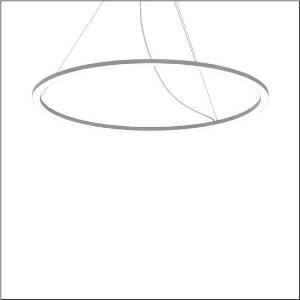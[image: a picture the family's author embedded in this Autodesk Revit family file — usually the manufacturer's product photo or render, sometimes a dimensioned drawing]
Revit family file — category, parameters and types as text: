
# Revit family: silica_r__21_ring-d_5pjbd4d3204a_8650
name_source: partatom
category: Lighting Fixtures
units: mm (PartAtom-declared; Revit-internal decimal feet)

## family parameters
Cut with Voids When Loaded = No
Host = Face
Light Source = No
Part Type = Normal
Room Calculation Point = No
Round Connector Dimension = Use Diameter
Shared = No

## types (1)
- Silica® 21 Ring-D (1 x LED, 11350 lm, 125 W, 4000K)
    Apparent Load = 125 VA
    CIE Flux Codes = 37 69 92 100 100
    Color Rendering = 80
    Color Temperature = 4000K
    Default Elevation = 1800 mm
    Description = Silica® 21 Ring-D, suspended luminaire, of PMMA, frosted, light emission: ring underside luminous distribution, primary light characteristic: symmetric, installation type: suspended mounting, LED, rated luminous flux: 11.350lm, luminous efficacy: 91lm/W, light colour: 840, colour temperature: 4000K, with terminal, 5-pole, mains connection: 230V, AC/DC, 0/50..60Hz, rated input power: 125W, housing, of extruded aluminium section, metallic grey (RAL 9006), diameter: 1.450mm, ceiling canopy, metallic grey (RAL 9006), protection rating (lamp compartment): IP40, insulation class (complete): insulation class I (protective earthing), certification: CE, impact resistance: IK02, permissible operating ambient temperature: 0..+35°C, packaging unit: 1 piece
    Height = 25 mm  [stored 0.082021 ft]
    Lamp = 1 x LED
    Lamp Light Flux = 11350 lm
    Lamp Power = 125 W
    Lamp count = 1
    Length = 1450 mm
    Luminous efficacy = 91 lm/W
    Manufacturer = Siteco
    ModVariant = No
    Model = 5PJBD4D3204A
    Mounting Place = Ceiling
    Mounting Type = Pendant
    Number of Poles = 1
    OnlyDefault = Yes
    Power Factor = 1
    Product Name = Silica® 21 Ring-D
    Product group = suspended luminaire
    ProductGroupID = 904
    Protection Class = Protection class I
    Protection Degree = IP 40
    RLX_Detail_Level = 1
    RLX_Emergency_Light_Flux = 0 lm
    RLX_Emergency_Type = 0
    RLX_Emergency_Type_DB = No
    RlxData = <blob elided: 17913 chars, md5=cb68c245>
    Socket = socket
    Standby Power = 0 W
    System Light Flux = 11350 lm
    System Power = 125 W
    Type Comments = Product without accessories
    Type Image = l_1251748.jpg
    URL = http://relux.com
    VarID = ---
    Voltage = 0 V
    Weight = 0.00 kg
    Width = 0 mm  [stored 0 ft]

note: [stored X ft] marks values corroborated as IEEE doubles in the binary element streams (Revit-internal decimal feet)

## geometry (parser evidence)
native form markers: Blend x4, Sweep x9
no freeform markers — native parametric forms only
